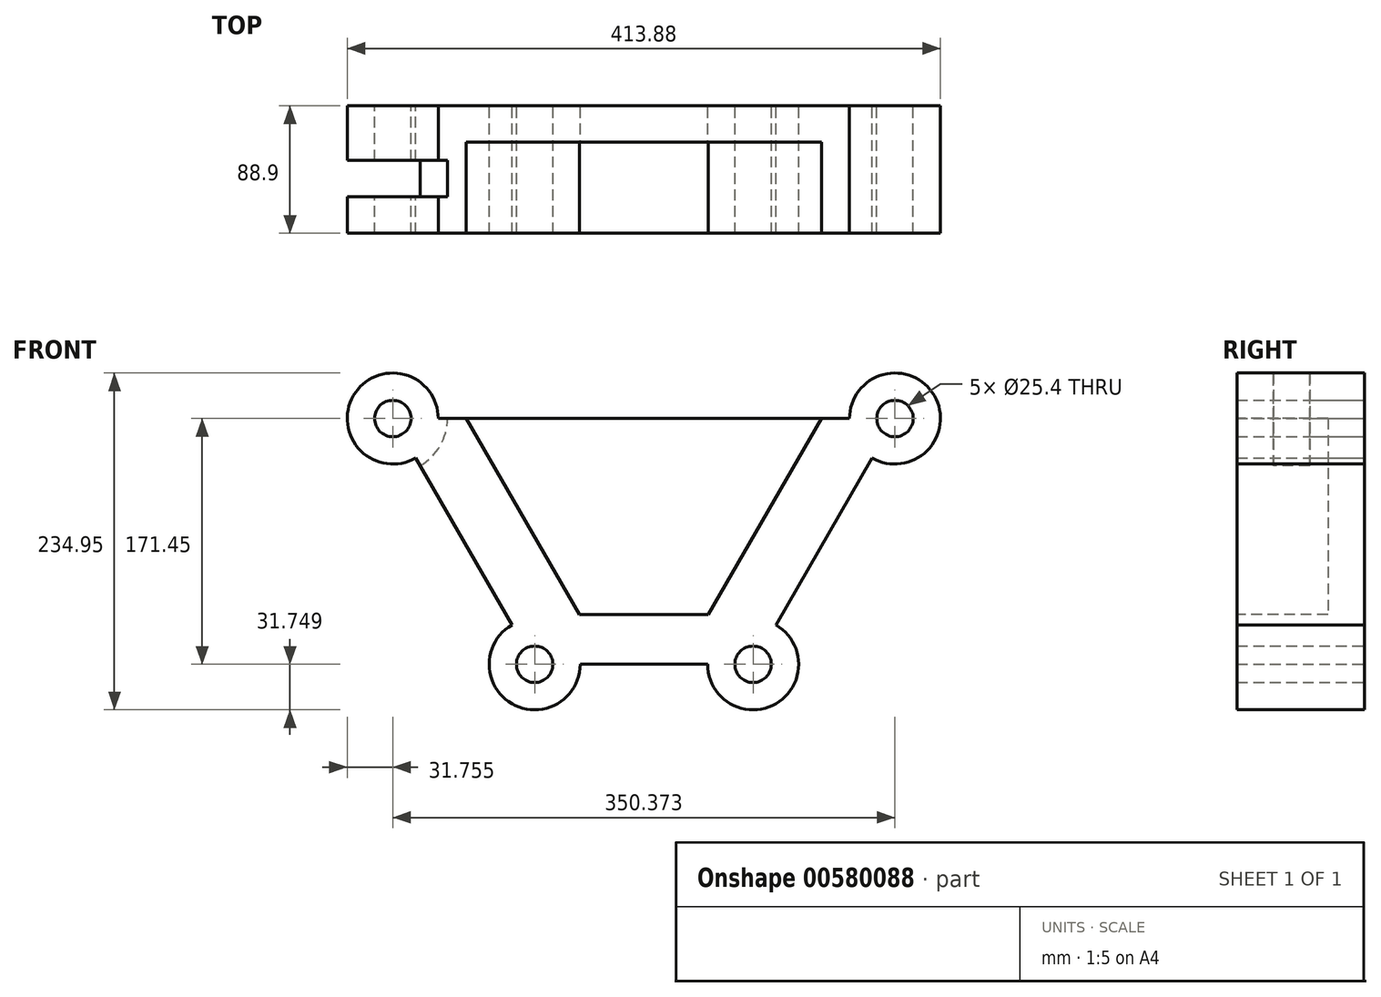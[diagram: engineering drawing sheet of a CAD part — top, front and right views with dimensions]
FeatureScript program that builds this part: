
annotation { "Feature Type Name" : "Feature", "Feature Type Description" : "" }
export const myFeature = defineFeature(function(context is Context, id is Id, definition is map)
    precondition{}
    {
        {
            var Q0;
            Q0=qCreatedBy(makeId("Front.planeOp"),FACE);
            var sketch = newSketch(context, id + "F0", { "sketchPlane" : qUnion([Q0])});
            skLineSegment(sketch, "E0", {"start": v(-63.64, -75.33) * mm, "end": v(88.76, -75.33) * mm});
            skLineSegment(sketch, "E1", {"start": v(-63.64, -75.33) * mm, "end": v(-162.63, 96.12) * mm});
            skLineSegment(sketch, "E2", {"start": v(-162.63, 96.12) * mm, "end": v(187.75, 96.12) * mm});
            skLineSegment(sketch, "E3", {"start": v(187.75, 96.12) * mm, "end": v(88.76, -75.33) * mm});
            skCircle(sketch, "E4", {"center": v(-63.64, -75.33) * mm, "radius": 12.7 * mm});
            skCircle(sketch, "E5", {"center": v(88.76, -75.33) * mm, "radius": 12.7 * mm});
            skCircle(sketch, "E6", {"center": v(-162.63, 96.12) * mm, "radius": 12.7 * mm});
            skCircle(sketch, "E7", {"center": v(187.75, 96.12) * mm, "radius": 12.7 * mm});
            skCircle(sketch, "E8", {"center": v(187.75, 96.12) * mm, "radius": 31.75 * mm});
            skCircle(sketch, "E9", {"center": v(88.76, -75.33) * mm, "radius": 31.75 * mm});
            skCircle(sketch, "E10", {"center": v(-63.64, -75.33) * mm, "radius": 31.75 * mm});
            skCircle(sketch, "E11", {"center": v(-162.63, 96.12) * mm, "radius": 31.75 * mm});
            skSolve(sketch);
        }
        {
            var Q0;
            {var subQ0=sQuery(id+"F0.wireOp",EDGE,"E11");var subQ1=sQuery(id+"F0.wireOp",EDGE,"E1");var subQ2=makeQuery(id+"F0.imprint","INTERSECT",VERTEX,{"derivedFrom":[subQ1,subQ0]});Q0=makeQuery(id+"F0.imprint","IMPRINT",FACE,{"disambiguationData":[TD([[makeQuery(id+"F0.imprint","IMPRINT",EDGE,{"disambiguationData":[TD([[subQ2,-1.0]])],"derivedFrom":subQ1}),1.0]])]});}
            var Q1;
            {var subQ0=sQuery(id+"F0.wireOp",EDGE,"E11");var subQ1=sQuery(id+"F0.wireOp",EDGE,"E1");var subQ2=makeQuery(id+"F0.imprint","INTERSECT",VERTEX,{"derivedFrom":[subQ1,subQ0]});Q1=makeQuery(id+"F0.imprint","IMPRINT",FACE,{"disambiguationData":[TD([[makeQuery(id+"F0.imprint","IMPRINT",EDGE,{"disambiguationData":[TD([[subQ2,-1.0]])],"derivedFrom":subQ1}),-1.0]])]});}
            var Q2;
            {var subQ0=sQuery(id+"F0.wireOp",EDGE,"E8");var subQ1=sQuery(id+"F0.wireOp",EDGE,"E2");var subQ2=makeQuery(id+"F0.imprint","INTERSECT",VERTEX,{"derivedFrom":[subQ1,subQ0]});Q2=makeQuery(id+"F0.imprint","IMPRINT",FACE,{"disambiguationData":[TD([[makeQuery(id+"F0.imprint","IMPRINT",EDGE,{"disambiguationData":[TD([[subQ2,-1.0]])],"derivedFrom":subQ1}),1.0]])]});}
            var Q3;
            {var subQ9=sQuery(id+"F0.wireOp",EDGE,"E10");var subQ13=sQuery(id+"F0.wireOp",EDGE,"E0");var subQ14=makeQuery(id+"F0.imprint","INTERSECT",VERTEX,{"derivedFrom":[subQ13,subQ9]});Q3=makeQuery(id+"F0.imprint","IMPRINT",FACE,{"disambiguationData":[TD([[makeQuery(id+"F0.imprint","IMPRINT",EDGE,{"disambiguationData":[TD([[subQ14,-1.0]])],"derivedFrom":subQ13}),1.0]])]});}
            var Q4;
            {var subQ0=sQuery(id+"F0.wireOp",EDGE,"E9");var subQ1=sQuery(id+"F0.wireOp",EDGE,"E0");var subQ2=makeQuery(id+"F0.imprint","INTERSECT",VERTEX,{"derivedFrom":[subQ1,subQ0]});Q4=makeQuery(id+"F0.imprint","IMPRINT",FACE,{"disambiguationData":[TD([[makeQuery(id+"F0.imprint","IMPRINT",EDGE,{"disambiguationData":[TD([[subQ2,-1.0]])],"derivedFrom":subQ1}),-1.0]])]});}
            var Q5;
            {var subQ0=sQuery(id+"F0.wireOp",EDGE,"E9");var subQ1=sQuery(id+"F0.wireOp",EDGE,"E0");var subQ2=makeQuery(id+"F0.imprint","INTERSECT",VERTEX,{"derivedFrom":[subQ1,subQ0]});Q5=makeQuery(id+"F0.imprint","IMPRINT",FACE,{"disambiguationData":[TD([[makeQuery(id+"F0.imprint","IMPRINT",EDGE,{"disambiguationData":[TD([[subQ2,-1.0]])],"derivedFrom":subQ1}),1.0]])]});}
            var Q6;
            {var subQ0=sQuery(id+"F0.wireOp",EDGE,"E10");var subQ1=sQuery(id+"F0.wireOp",EDGE,"E0");var subQ2=makeQuery(id+"F0.imprint","INTERSECT",VERTEX,{"derivedFrom":[subQ1,subQ0]});Q6=makeQuery(id+"F0.imprint","IMPRINT",FACE,{"disambiguationData":[TD([[makeQuery(id+"F0.imprint","IMPRINT",EDGE,{"disambiguationData":[TD([[subQ2,1.0]])],"derivedFrom":subQ1}),-1.0]])]});}
            var Q7;
            {var subQ0=sQuery(id+"F0.wireOp",EDGE,"E10");var subQ1=sQuery(id+"F0.wireOp",EDGE,"E0");var subQ2=makeQuery(id+"F0.imprint","INTERSECT",VERTEX,{"derivedFrom":[subQ1,subQ0]});Q7=makeQuery(id+"F0.imprint","IMPRINT",FACE,{"disambiguationData":[TD([[makeQuery(id+"F0.imprint","IMPRINT",EDGE,{"disambiguationData":[TD([[subQ2,1.0]])],"derivedFrom":subQ1}),1.0]])]});}
            var Q8;
            {var subQ0=sQuery(id+"F0.wireOp",EDGE,"E8");var subQ1=sQuery(id+"F0.wireOp",EDGE,"E2");var subQ2=makeQuery(id+"F0.imprint","INTERSECT",VERTEX,{"derivedFrom":[subQ1,subQ0]});Q8=makeQuery(id+"F0.imprint","IMPRINT",FACE,{"disambiguationData":[TD([[makeQuery(id+"F0.imprint","IMPRINT",EDGE,{"disambiguationData":[TD([[subQ2,-1.0]])],"derivedFrom":subQ1}),-1.0]])]});}
            extrude(context, id + "F1", {"entities" : qUnion([Q0, Q1, Q2, Q3, Q4, Q5, Q6, Q7, Q8]), "endBound" : BoundingType.SYMMETRIC, "depth" : 101.6 * mm, "offsetDistance" : 25.4 * mm});
        }
        {
            var Q0;
            Q0=makeQuery(id+"F1.opExtrude","CAP_FACE",FACE,{"disambiguationData":[OSD([sQuery(id+"F0.wireOp",EDGE,"E0"),sQuery(id+"F0.wireOp",EDGE,"E1"),sQuery(id+"F0.wireOp",EDGE,"E2"),sQuery(id+"F0.wireOp",EDGE,"E3"),sQuery(id+"F0.wireOp",EDGE,"E4"),sQuery(id+"F0.wireOp",EDGE,"E5"),sQuery(id+"F0.wireOp",EDGE,"E6"),sQuery(id+"F0.wireOp",EDGE,"E7"),sQuery(id+"F0.wireOp",EDGE,"E8"),sQuery(id+"F0.wireOp",EDGE,"E9"),sQuery(id+"F0.wireOp",EDGE,"E10"),sQuery(id+"F0.wireOp",EDGE,"E11")])],"isStart":false});
            var sketch = newSketch(context, id + "F2", { "sketchPlane" : qUnion([Q0])});
            skLineSegment(sketch, "E12", {"start": v(-111.3, 96.12) * mm, "end": v(-32.32, -40.68) * mm});
            skLineSegment(sketch, "E13", {"start": v(-32.32, -40.68) * mm, "end": v(57.44, -40.68) * mm});
            skLineSegment(sketch, "E14", {"start": v(57.44, -40.68) * mm, "end": v(136.42, 96.12) * mm});
            skLineSegment(sketch, "E15", {"start": v(136.42, 96.12) * mm, "end": v(-111.3, 96.12) * mm});
            skSolve(sketch);
        }
        {
            var Q0;
            Q0=makeQuery(id+"F2.imprint","IMPRINT",FACE,{"disambiguationData":[TD([[makeQuery(id+"F2.imprint","IMPRINT",EDGE,{"derivedFrom":sQuery(id+"F2.wireOp",EDGE,"E12")}),1.0]])]});
            extrude(context, id + "F3", {"entities" : qUnion([Q0]), "operationType" : NewBodyOperationType.REMOVE, "oppositeDirection" : true, "depth" : 76.2 * mm, "offsetDistance" : 25.4 * mm});
        }
        {
            var Q0;
            Q0=qCreatedBy(makeId("Front.planeOp"),FACE);
            var sketch = newSketch(context, id + "F4", { "sketchPlane" : qUnion([Q0])});
            skCircle(sketch, "E16", {"center": v(-162.63, 96.12) * mm, "radius": 38.1 * mm});
            skCircle(sketch, "E17", {"center": v(187.75, 96.12) * mm, "radius": 38.1 * mm});
            skCircle(sketch, "E18", {"center": v(-63.64, -75.33) * mm, "radius": 38.1 * mm});
            skCircle(sketch, "E19", {"center": v(88.76, -75.33) * mm, "radius": 38.1 * mm});
            skSolve(sketch);
        }
        {
            var Q0;
            Q0=makeQuery(id+"F4.imprint","IMPRINT",FACE,{"disambiguationData":[TD([[makeQuery(id+"F4.imprint","IMPRINT",EDGE,{"derivedFrom":sQuery(id+"F4.wireOp",EDGE,"E16")}),1.0]])]});
            var Q1;
            Q1=makeQuery(id+"F1.opExtrude","CAP_FACE",FACE,{"disambiguationData":[OSD([sQuery(id+"F0.wireOp",EDGE,"E0"),sQuery(id+"F0.wireOp",EDGE,"E1"),sQuery(id+"F0.wireOp",EDGE,"E2"),sQuery(id+"F0.wireOp",EDGE,"E3"),sQuery(id+"F0.wireOp",EDGE,"E4"),sQuery(id+"F0.wireOp",EDGE,"E5"),sQuery(id+"F0.wireOp",EDGE,"E6"),sQuery(id+"F0.wireOp",EDGE,"E7"),sQuery(id+"F0.wireOp",EDGE,"E8"),sQuery(id+"F0.wireOp",EDGE,"E9"),sQuery(id+"F0.wireOp",EDGE,"E10"),sQuery(id+"F0.wireOp",EDGE,"E11")])],"isStart":false});
            extrude(context, id + "F5", {"entities" : qUnion([Q0, Q1]), "operationType" : NewBodyOperationType.REMOVE, "endBound" : BoundingType.SYMMETRIC, "oppositeDirection" : true, "depth" : 25.4 * mm, "offsetDistance" : 25.4 * mm});
        }
    });
